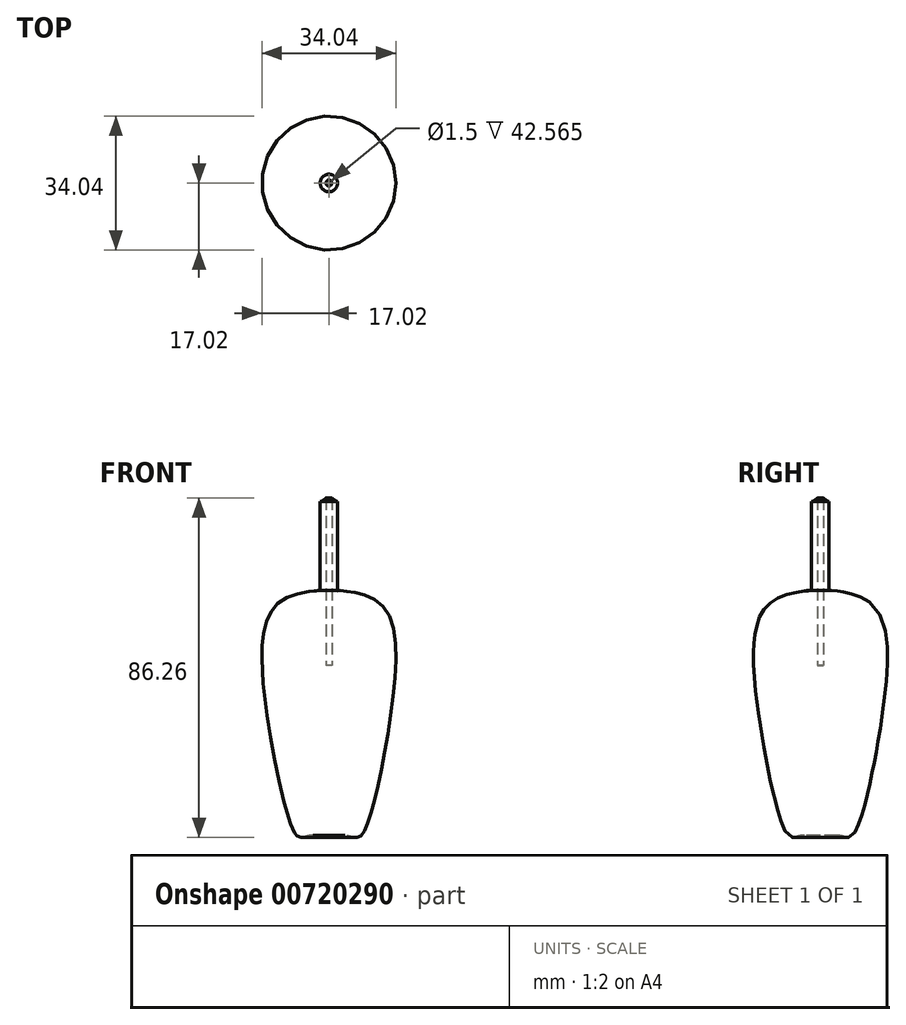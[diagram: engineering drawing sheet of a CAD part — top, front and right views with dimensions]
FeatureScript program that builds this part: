
annotation { "Feature Type Name" : "Feature", "Feature Type Description" : "" }
export const myFeature = defineFeature(function(context is Context, id is Id, definition is map)
    precondition{}
    {
        {
            var Q0;
            Q0=qCreatedBy(makeId("Front.planeOp"),FACE);
            var sketch = newSketch(context, id + "F0", { "sketchPlane" : qUnion([Q0])});
            skLineSegment(sketch, "E0", {"start": v(0, 85.98) * mm, "end": v(0, -52.41) * mm});
            skFitSpline(sketch, "E1", {"points": [v(0, -43.01) * mm, v(4.88, -43.19) * mm, v(7.46, -43.67) * mm, v(9.84, -40) * mm, v(15.7, -12.68) * mm, v(13.95, 14.77) * mm, v(4.17, 18.89) * mm, v(2.22, 18.89) * mm, v(2.22, 18.71) * mm, v(2.4, 18.71) * mm], "startDerivative": vector(57.83, -13.3) * mm, "endDerivative": vector(10.38, 2.41) * mm});
            skLineSegment(sketch, "E2", {"start": v(2.22, 18.89) * mm, "end": v(2.22, 41.61) * mm});
            skFitSpline(sketch, "E3", {"points": [v(0, 43.33) * mm, v(18.06, 54.8) * mm, v(9.06, 72.21) * mm, v(0, 71.96) * mm, v(0, 71.96) * mm], "startDerivative": vector(43.51, -51.6) * mm, "endDerivative": vector(0.61, 0.93) * mm});
            skPoint(sketch, "E4.end.orphan", {"position": v(0, 47.62) * mm});
            skSolve(sketch);
        }
        {
            var Q0;
            {var subQ4=sQuery(id+"F0.wireOp",EDGE,"E2");Q0=makeQuery(id+"F0.imprint","IMPRINT",FACE,{"disambiguationData":[TD([[makeQuery(id+"F0.imprint","IMPRINT",EDGE,{"derivedFrom":subQ4}),1.0]])]});}
            var Q1;
            {var subQ0=sQuery(id+"F0.wireOp",EDGE,"E3");var subQ1=sQuery(id+"F0.wireOp",EDGE,"E0");var subQ2=makeQuery(id+"F0.imprint","INTERSECT",VERTEX,{"disambiguationData":[OD(0.0)],"derivedFrom":[subQ1,subQ0]});Q1=makeQuery(id+"F0.imprint","IMPRINT",FACE,{"disambiguationData":[TD([[makeQuery(id+"F0.imprint","IMPRINT",EDGE,{"disambiguationData":[TD([[subQ2,1.0]])],"derivedFrom":subQ1}),1.0]])]});}
            var Q2;
            Q2=sQuery(id+"F0.wireOp",EDGE,"E0");
            revolve(context, id + "F1", {"surfaceOperationType" : NewSurfaceOperationType.NEW, "entities" : qUnion([Q0, Q1]), "axis" : qUnion([Q2]), "revolveType" : RevolveType.FULL});
        }
        {
            var Q0;
            Q0=qCreatedBy(makeId("Top.planeOp"),FACE);
            cPlane(context, id + "F2", {"entities" : qUnion([Q0]), "cplaneType" : CPlaneType.OFFSET, "offset" : 76.3 * mm, "width" : 150 * mm, "height" : 150 * mm});
        }
        {
            var Q0;
            Q0=qCreatedBy(id+"F2.planeOp",FACE);
            var sketch = newSketch(context, id + "F3", { "sketchPlane" : qUnion([Q0])});
            skCircle(sketch, "E5", {"center": v(0, 0) * mm, "radius": 12.82 * mm});
            skSolve(sketch);
        }
        {
            var Q0;
            Q0 = qSketchRegion(id + "F3", true);
            extrude(context, id + "F4", {"entities" : qUnion([Q0]), "operationType" : NewBodyOperationType.REMOVE, "oppositeDirection" : true, "depth" : 30.4 * mm, "offsetDistance" : 25 * mm});
        }
        {
            var Q0;
            Q0=qCreatedBy(makeId("Top.planeOp"),FACE);
            var sketch = newSketch(context, id + "F5", { "sketchPlane" : qUnion([Q0])});
            skCircle(sketch, "E6", {"center": v(0, 0) * mm, "radius": 0.75 * mm});
            skSolve(sketch);
        }
        {
            var Q0;
            Q0 = qSketchRegion(id + "F5", true);
            extrude(context, id + "F6", {"entities" : qUnion([Q0]), "operationType" : NewBodyOperationType.REMOVE, "depth" : 72 * mm, "offsetDistance" : 25 * mm});
        }
    });
